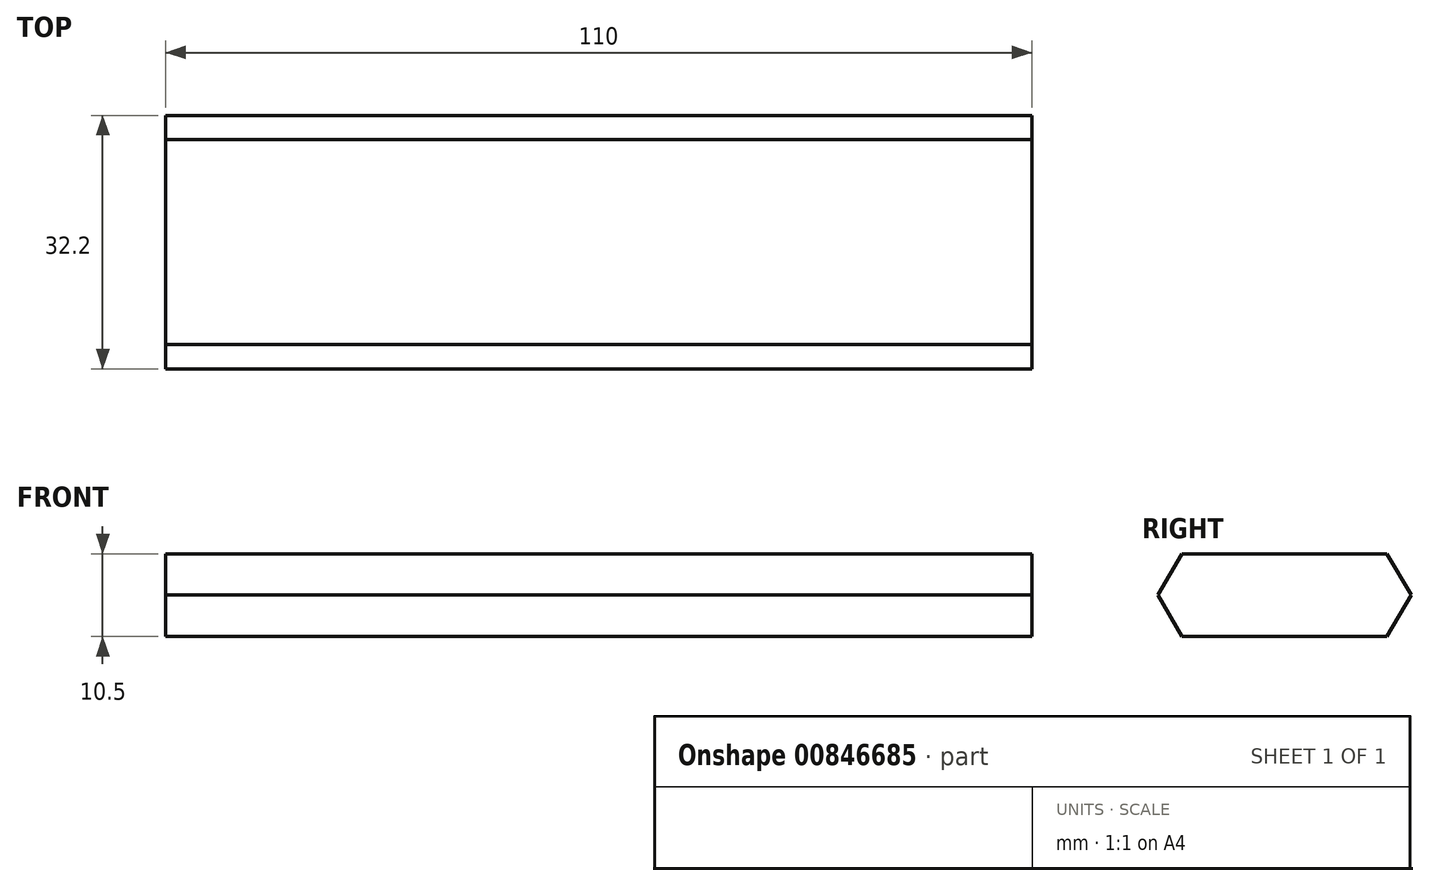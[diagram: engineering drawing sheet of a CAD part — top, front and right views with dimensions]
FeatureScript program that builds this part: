
annotation { "Feature Type Name" : "Feature", "Feature Type Description" : "" }
export const myFeature = defineFeature(function(context is Context, id is Id, definition is map)
    precondition{}
    {
        {
            var Q0;
            Q0=qCreatedBy(makeId("Right.planeOp"),FACE);
            var sketch = newSketch(context, id + "F0", { "sketchPlane" : qUnion([Q0])});
            skLineSegment(sketch, "E0.bottom", {"start": v(13, -5.25) * mm, "end": v(-13, -5.25) * mm});
            skLineSegment(sketch, "E0.top", {"start": v(13, 5.25) * mm, "end": v(-13, 5.25) * mm});
            skPoint(sketch, "E0.middle", {"position": v(0, 0) * mm});
            skLineSegment(sketch, "E1", {"start": v(-13, 5.25) * mm, "end": v(-16.1, 0) * mm});
            skLineSegment(sketch, "E2", {"start": v(-16.1, 0) * mm, "end": v(-13, -5.25) * mm});
            skLineSegment(sketch, "E3.MirrorCS", {"start": v(16.1, 0) * mm, "end": v(13, -5.25) * mm});
            skLineSegment(sketch, "E4.MirrorCS", {"start": v(13, 5.25) * mm, "end": v(16.1, 0) * mm});
            skSolve(sketch);
        }
        {
            var Q0;
            Q0=makeQuery(id+"F0.imprint","IMPRINT",FACE,{"disambiguationData":[TD([[makeQuery(id+"F0.imprint","IMPRINT",EDGE,{"derivedFrom":sQuery(id+"F0.wireOp",EDGE,"E0.bottom")}),-1.0]])]});
            extrude(context, id + "F1", {"entities" : qUnion([Q0]), "endBound" : BoundingType.SYMMETRIC, "depth" : 110 * mm, "offsetDistance" : 25 * mm});
        }
    });
